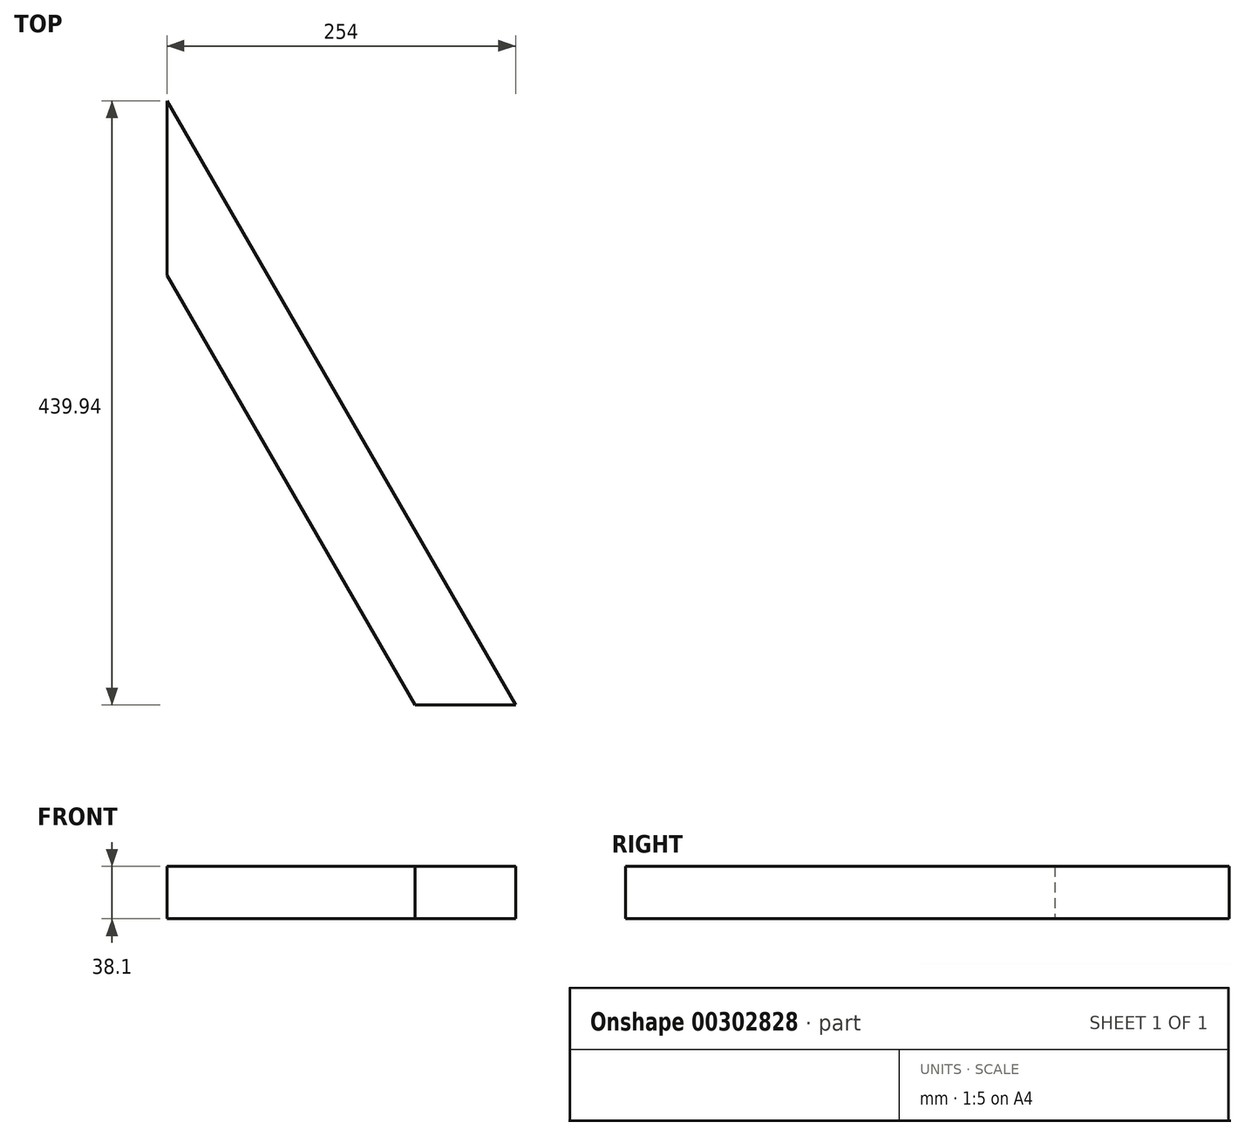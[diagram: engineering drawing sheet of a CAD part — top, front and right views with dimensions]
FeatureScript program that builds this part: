
annotation { "Feature Type Name" : "Feature", "Feature Type Description" : "" }
export const myFeature = defineFeature(function(context is Context, id is Id, definition is map)
    precondition{}
    {
        {
            var Q0;
            Q0=qCreatedBy(makeId("Top.planeOp"),FACE);
            var sketch = newSketch(context, id + "F0", { "sketchPlane" : qUnion([Q0])});
            skLineSegment(sketch, "E0", {"start": v(0, 0) * mm, "end": v(0, 439.94) * mm, "construction": true});
            skLineSegment(sketch, "E1", {"start": v(0, 439.94) * mm, "end": v(254, 0) * mm, "construction": true});
            skLineSegment(sketch, "E2", {"start": v(254, 0) * mm, "end": v(0, 0) * mm, "construction": true});
            skLineSegment(sketch, "E3", {"start": v(0, 439.94) * mm, "end": v(254, 0) * mm});
            skLineSegment(sketch, "E4", {"start": v(180.68, 0) * mm, "end": v(0, 312.94) * mm});
            skLineSegment(sketch, "E5", {"start": v(0, 312.94) * mm, "end": v(0, 439.94) * mm});
            skLineSegment(sketch, "E6", {"start": v(254, 0) * mm, "end": v(180.68, 0) * mm});
            skSolve(sketch);
        }
        {
            var Q0;
            Q0 = qSketchRegion(id + "F0", true);
            extrude(context, id + "F1", {"entities" : qUnion([Q0]), "endBound" : BoundingType.SYMMETRIC, "depth" : 38.1 * mm});
        }
    });
